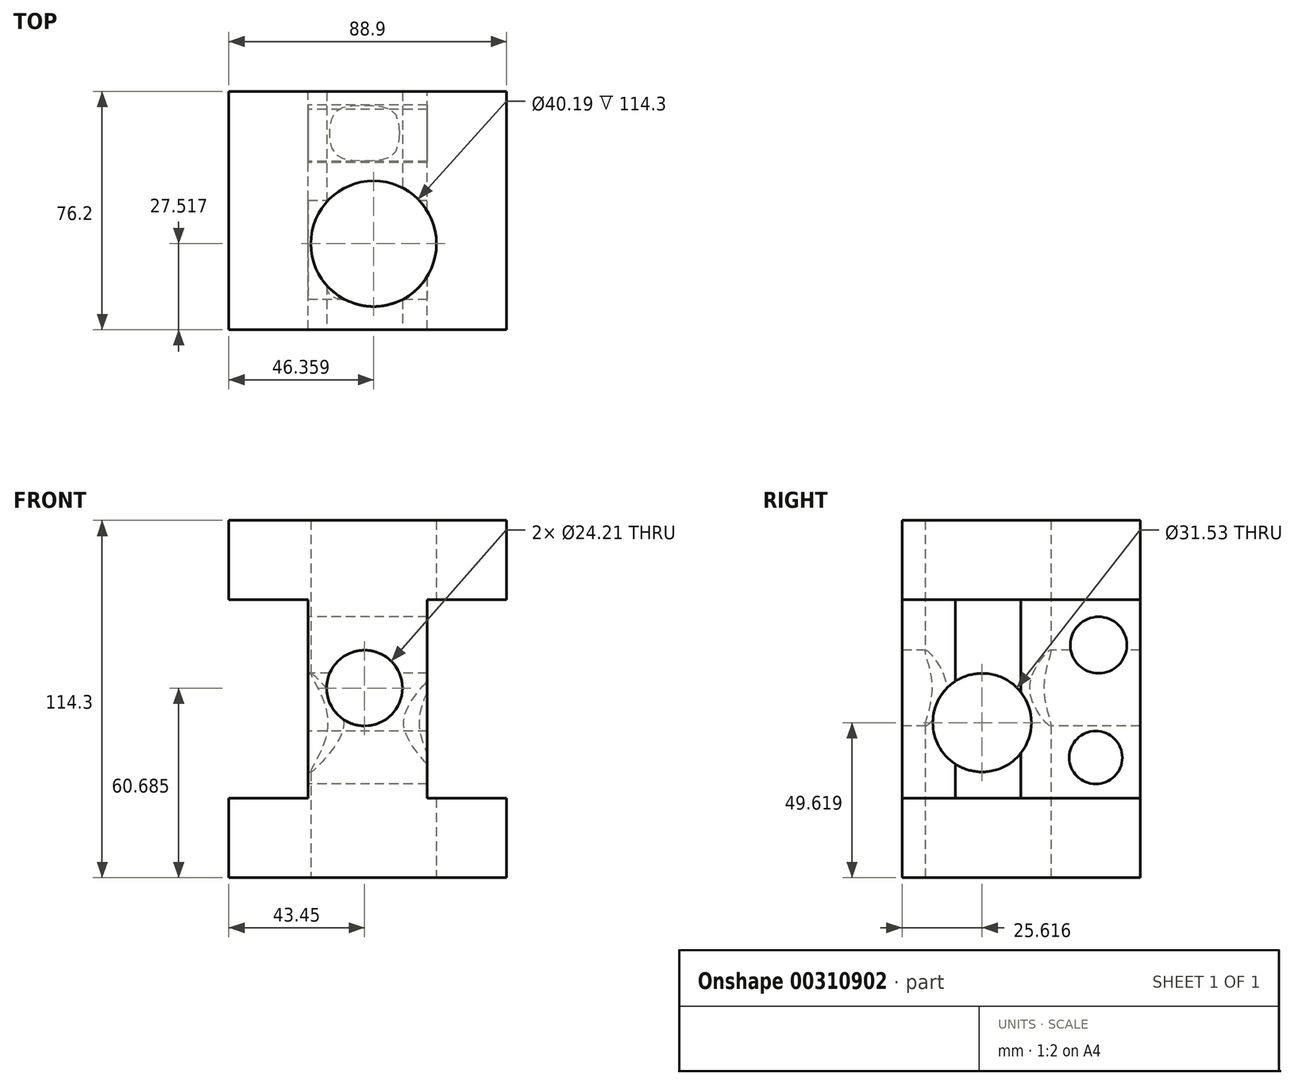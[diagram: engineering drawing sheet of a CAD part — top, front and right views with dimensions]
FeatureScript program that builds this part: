
annotation { "Feature Type Name" : "Feature", "Feature Type Description" : "" }
export const myFeature = defineFeature(function(context is Context, id is Id, definition is map)
    precondition{}
    {
        {
            var Q0;
            Q0=qCreatedBy(makeId("Front.planeOp"),FACE);
            var sketch = newSketch(context, id + "F0", { "sketchPlane" : qUnion([Q0])});
            skLineSegment(sketch, "E0", {"start": v(-39.34, -55.32) * mm, "end": v(49.56, -55.32) * mm});
            skLineSegment(sketch, "E1", {"start": v(49.56, -29.92) * mm, "end": v(49.56, -55.32) * mm});
            skLineSegment(sketch, "E2", {"start": v(49.56, -29.92) * mm, "end": v(24.16, -29.92) * mm});
            skLineSegment(sketch, "E3", {"start": v(24.16, -29.92) * mm, "end": v(24.16, 33.58) * mm});
            skLineSegment(sketch, "E4", {"start": v(24.16, 33.58) * mm, "end": v(49.56, 33.58) * mm});
            skLineSegment(sketch, "E5", {"start": v(49.56, 33.58) * mm, "end": v(49.56, 58.98) * mm});
            skLineSegment(sketch, "E6", {"start": v(49.56, 58.98) * mm, "end": v(-39.34, 58.98) * mm});
            skLineSegment(sketch, "E7", {"start": v(-39.34, 58.98) * mm, "end": v(-39.34, 33.58) * mm});
            skLineSegment(sketch, "E8", {"start": v(-39.34, 33.58) * mm, "end": v(-13.94, 33.58) * mm});
            skLineSegment(sketch, "E9", {"start": v(-13.94, 33.58) * mm, "end": v(-13.94, -29.92) * mm});
            skLineSegment(sketch, "E10", {"start": v(-13.94, -29.92) * mm, "end": v(-39.34, -29.92) * mm});
            skLineSegment(sketch, "E11", {"start": v(-39.34, -29.92) * mm, "end": v(-39.34, -55.32) * mm});
            skSolve(sketch);
        }
        {
            var Q0;
            Q0 = qSketchRegion(id + "FOpWsHZ9HblcvBN_0", true);
            var Q1;
            Q1=makeQuery(id+"F0.imprint","IMPRINT",FACE,{"disambiguationData":[TD([[makeQuery(id+"F0.imprint","IMPRINT",EDGE,{"derivedFrom":sQuery(id+"F0.wireOp",EDGE,"E0")}),1.0]])]});
            var Q2;
            Q2=makeQuery(id+"FdLfwzUYXAjQrJY_0.imprint","IMPRINT",FACE,{"disambiguationData":[TD([[makeQuery(id+"FdLfwzUYXAjQrJY_0.imprint","IMPRINT",EDGE,{"derivedFrom":makeQuery(id+"F0.imprint","IMPRINT",EDGE,{"derivedFrom":sQuery(id+"F0.wireOp",EDGE,"E0")})}),1.0]])]});
            extrude(context, id + "F1", {"entities" : qUnion([Q0, Q1, Q2]), "depth" : 76.2 * mm});
        }
        {
            var Q0;
            {var subQ0=sQuery(id+"F0.wireOp",EDGE,"E3");Q0=makeQuery(id+"F1.opExtrude","SWEPT_FACE",FACE,{"disambiguationData":[OSD([subQ0]),TDD([makeQuery(id+"F0.imprint","IMPRINT",EDGE,{"derivedFrom":subQ0})])]});}
            var sketch = newSketch(context, id + "F2", { "sketchPlane" : qUnion([Q0])});
            skCircle(sketch, "E12", {"center": v(-50.58, -5.7) * mm, "radius": 15.77 * mm});
            skPoint(sketch, "E12.first.point", {"position": v(-42.1, 7.58) * mm});
            skPoint(sketch, "E12.second.point", {"position": v(-66.24, -7.58) * mm});
            skPoint(sketch, "E12.third.point", {"position": v(-40.86, -18.1) * mm});
            skSolve(sketch);
        }
        {
            var Q0;
            Q0=makeQuery(id+"F2.imprint","IMPRINT",FACE,{"disambiguationData":[TD([[makeQuery(id+"F2.imprint","IMPRINT",EDGE,{"derivedFrom":sQuery(id+"F2.wireOp",EDGE,"E12")}),1.0]])]});
            extrude(context, id + "F3", {"entities" : qUnion([Q0]), "operationType" : NewBodyOperationType.REMOVE, "endBound" : BoundingType.THROUGH_ALL, "oppositeDirection" : true, "depth" : 25.4 * mm});
        }
        {
            var Q0;
            Q0=makeQuery(id+"F1.opExtrude","SWEPT_FACE",FACE,{"disambiguationData":[OSD([sQuery(id+"F0.wireOp",EDGE,"E9")])]});
            var sketch = newSketch(context, id + "F4", { "sketchPlane" : qUnion([Q0])});
            skCircle(sketch, "E13", {"center": v(14.2, -16.88) * mm, "radius": 8.48 * mm});
            skPoint(sketch, "E13.first.point", {"position": v(17.64, -9.13) * mm});
            skPoint(sketch, "E13.second.point", {"position": v(12.7, -25.23) * mm});
            skPoint(sketch, "E13.third.point", {"position": v(21.98, -20.27) * mm});
            skSolve(sketch);
        }
        {
            var Q0;
            Q0=makeQuery(id+"F4.imprint","IMPRINT",FACE,{"disambiguationData":[TD([[makeQuery(id+"F4.imprint","IMPRINT",EDGE,{"derivedFrom":sQuery(id+"F4.wireOp",EDGE,"E13")}),1.0]])]});
            extrude(context, id + "F5", {"entities" : qUnion([Q0]), "operationType" : NewBodyOperationType.REMOVE, "oppositeDirection" : true, "depth" : 101.6 * mm});
        }
        {
            var Q0;
            Q0=makeQuery(id+"F1.opExtrude","SWEPT_FACE",FACE,{"disambiguationData":[OSD([sQuery(id+"F0.wireOp",EDGE,"E9")])]});
            var sketch = newSketch(context, id + "F6", { "sketchPlane" : qUnion([Q0])});
            skCircle(sketch, "E14", {"center": v(13.32, 19.12) * mm, "radius": 9.04 * mm});
            skSolve(sketch);
        }
        {
            var Q0;
            Q0=makeQuery(id+"F6.imprint","IMPRINT",FACE,{"disambiguationData":[TD([[makeQuery(id+"F6.imprint","IMPRINT",EDGE,{"derivedFrom":sQuery(id+"F6.wireOp",EDGE,"E14")}),1.0]])]});
            extrude(context, id + "F7", {"entities" : qUnion([Q0]), "operationType" : NewBodyOperationType.REMOVE, "oppositeDirection" : true, "depth" : 101.6 * mm});
        }
        {
            var Q0;
            Q0=makeQuery(id+"F1.opExtrude","SWEPT_FACE",FACE,{"disambiguationData":[OSD([sQuery(id+"F0.wireOp",EDGE,"E0")])]});
            var sketch = newSketch(context, id + "F8", { "sketchPlane" : qUnion([Q0])});
            skCircle(sketch, "E15", {"center": v(7.02, 48.68) * mm, "radius": 20.1 * mm});
            skSolve(sketch);
        }
        {
            var Q0;
            Q0 = qSketchRegion(id + "F8", true);
            extrude(context, id + "F9", {"entities" : qUnion([Q0]), "operationType" : NewBodyOperationType.REMOVE, "oppositeDirection" : true, "depth" : 254 * mm});
        }
        {
            var Q0;
            Q0=makeQuery(id+"F1.opExtrude","CAP_FACE",FACE,{"disambiguationData":[OSD([sQuery(id+"F0.wireOp",EDGE,"E0"),sQuery(id+"F0.wireOp",EDGE,"E1"),sQuery(id+"F0.wireOp",EDGE,"E2"),sQuery(id+"F0.wireOp",EDGE,"E3"),sQuery(id+"F0.wireOp",EDGE,"E4"),sQuery(id+"F0.wireOp",EDGE,"E5"),sQuery(id+"F0.wireOp",EDGE,"E6"),sQuery(id+"F0.wireOp",EDGE,"E7"),sQuery(id+"F0.wireOp",EDGE,"E8"),sQuery(id+"F0.wireOp",EDGE,"E9"),sQuery(id+"F0.wireOp",EDGE,"E10"),sQuery(id+"F0.wireOp",EDGE,"E11")])],"isStart":false});
            var sketch = newSketch(context, id + "F10", { "sketchPlane" : qUnion([Q0])});
            skCircle(sketch, "E16", {"center": v(4.11, 5.37) * mm, "radius": 12.1 * mm});
            skSolve(sketch);
        }
        {
            var Q0;
            Q0=makeQuery(id+"F10.imprint","IMPRINT",FACE,{"disambiguationData":[TD([[makeQuery(id+"F10.imprint","IMPRINT",EDGE,{"derivedFrom":sQuery(id+"F10.wireOp",EDGE,"E16")}),1.0]])]});
            extrude(context, id + "F11", {"entities" : qUnion([Q0]), "operationType" : NewBodyOperationType.REMOVE, "oppositeDirection" : true, "depth" : 152.4 * mm});
        }
    });
